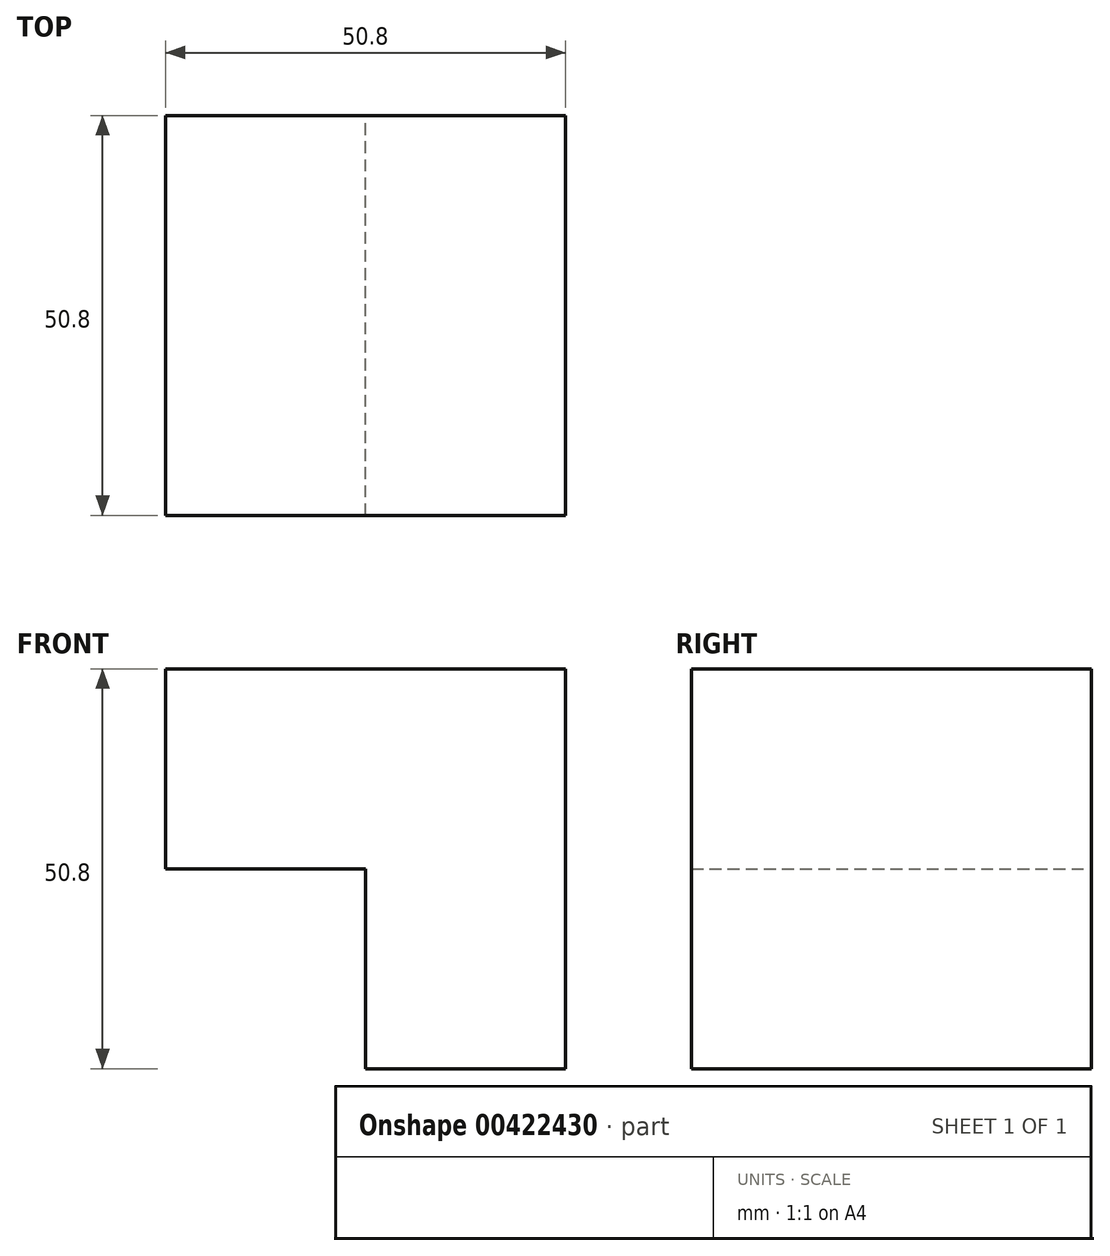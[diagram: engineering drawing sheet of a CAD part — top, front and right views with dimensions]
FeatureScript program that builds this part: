
annotation { "Feature Type Name" : "Feature", "Feature Type Description" : "" }
export const myFeature = defineFeature(function(context is Context, id is Id, definition is map)
    precondition{}
    {
        {
            var Q0;
            Q0=qCreatedBy(makeId("Front.planeOp"),FACE);
            var sketch = newSketch(context, id + "F0", { "sketchPlane" : qUnion([Q0])});
            skLineSegment(sketch, "E0", {"start": v(0, 0) * mm, "end": v(0, 50.8) * mm});
            skLineSegment(sketch, "E1", {"start": v(0, 50.8) * mm, "end": v(-50.8, 50.8) * mm});
            skLineSegment(sketch, "E2", {"start": v(-50.8, 50.8) * mm, "end": v(-50.8, 25.4) * mm});
            skLineSegment(sketch, "E3", {"start": v(-50.8, 25.4) * mm, "end": v(-25.4, 25.4) * mm});
            skLineSegment(sketch, "E4", {"start": v(-25.4, 25.4) * mm, "end": v(-25.4, 0) * mm});
            skLineSegment(sketch, "E5", {"start": v(-25.4, 0) * mm, "end": v(0, 0) * mm});
            skSolve(sketch);
        }
        {
            var Q0;
            Q0=makeQuery(id+"F0.imprint","IMPRINT",FACE,{"disambiguationData":[TD([[makeQuery(id+"F0.imprint","IMPRINT",EDGE,{"derivedFrom":sQuery(id+"F0.wireOp",EDGE,"E0")}),1.0]])]});
            extrude(context, id + "F1", {"entities" : qUnion([Q0]), "depth" : 50.8 * mm});
        }
    });
